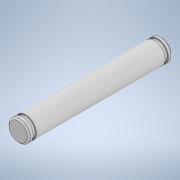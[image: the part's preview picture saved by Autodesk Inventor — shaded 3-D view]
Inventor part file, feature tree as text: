
AUTODESK INVENTOR PART (.ipt)
format: ipt  version: 2022 (Build 260153000, 153)  size: 120,320 bytes
history: native  units: mm
features: revolve x1, chamfer x1, sketch x1
ambient origin geometry x8: Origin, YZ Plane, XZ Plane, XY Plane, X Axis, Y Axis, Z Axis, Center Point
bodies: Solid1 (feature_tree)
feature tree (3):
  revolve  "Revolution1"  [1 undecoded]
  chamfer  "Chamfer1"  Distance=1.5mm
  sketch  "Sketch1"  dims[d0=5.0mm d3=60.0mm d4=1.5mm d5=0.5mm d6=1.5mm d7=2.0mm d8=2.0mm d9=90.0deg d10=0.75mm d11=2.0mm d12=45.0deg]
note: 1 required parameter value undecoded (feature->parameter linkage not recoverable at this tier; creation-order binding heuristic only, values carry confidence <= 0.55)
